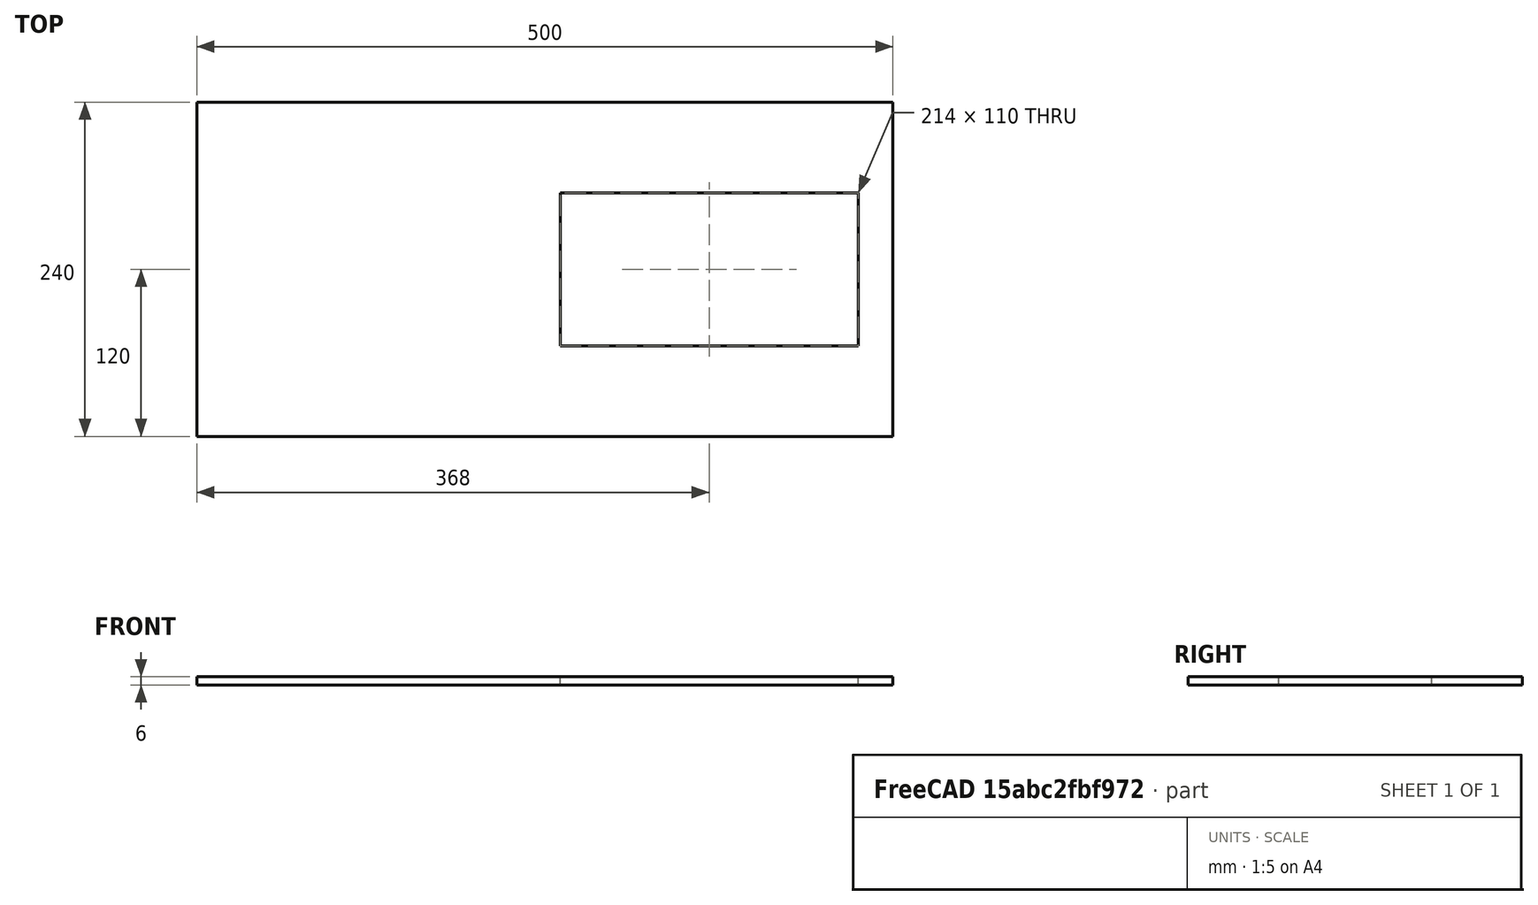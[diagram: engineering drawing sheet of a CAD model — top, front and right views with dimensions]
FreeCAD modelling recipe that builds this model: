
FCSTD DOCUMENT  (FreeCAD 0.18R4 (GitTag))
Label: cubierta_husillos
License: All rights reserved
LicenseURL: http://en.wikipedia.org/wiki/All_rights_reserved
objects: Sketcher::SketchObject×1, PartDesign::Pad×1, PartDesign::Body×1
note: 4 computed .brp shape members not serialized (recipe doc carries the construction recipe); baked Part::Feature solids carry a one-line shape summary decoded from their .brp

FEATURE [Sketcher::SketchObject] Sketch
  MapMode = 5
  Support = -> [XY_Plane]
  sketch-geometry (8):
    g0: LineSegment StartX=0 StartY=0 StartZ=0 EndX=500 EndY=0 EndZ=0
    g1: LineSegment StartX=500 StartY=0 StartZ=0 EndX=500 EndY=240 EndZ=0
    g2: LineSegment StartX=500 StartY=240 StartZ=0 EndX=0 EndY=240 EndZ=0
    g3: LineSegment StartX=0 StartY=240 StartZ=0 EndX=0 EndY=0 EndZ=0
    g4: LineSegment StartX=261 StartY=175 StartZ=0 EndX=475 EndY=175 EndZ=0
    g5: LineSegment StartX=475 StartY=175 StartZ=0 EndX=475 EndY=65 EndZ=0
    g6: LineSegment StartX=475 StartY=65 StartZ=0 EndX=261 EndY=65 EndZ=0
    g7: LineSegment StartX=261 StartY=65 StartZ=0 EndX=261 EndY=175 EndZ=0
  constraints (23):
    c: Coincident(g0,g1)
    c: Coincident(g1,g2)
    c: Coincident(g2,g3)
    c: Coincident(g3,g0)
    c: Horizontal(g0)
    c: Horizontal(g2)
    c: Vertical(g1)
    c: Vertical(g3)
    c: DistanceX(g0,g0) = 500
    c: Coincident(g0,g-1)
    c: DistanceY(g3,g3) = 240
    c: Coincident(g4,g5)
    c: Coincident(g5,g6)
    c: Coincident(g6,g7)
    c: Coincident(g7,g4)
    c: Horizontal(g4)
    c: Horizontal(g6)
    c: Vertical(g5)
    c: Vertical(g7)
    c: Distance(g4,g3) = 261
    c: Distance(g4,g1) = 25
    c: Distance(g6,g0) = 65
    c: Distance(g4,g2) = 65
FEATURE [PartDesign::Pad] Pad
  Length = 6
  Length2 = 100
  Profile = -> Sketch
  Type = 0
FEATURE [PartDesign::Body] Body
  Group = -> [Sketch,Pad]
  Origin = -> Origin
  Tip = -> Pad
